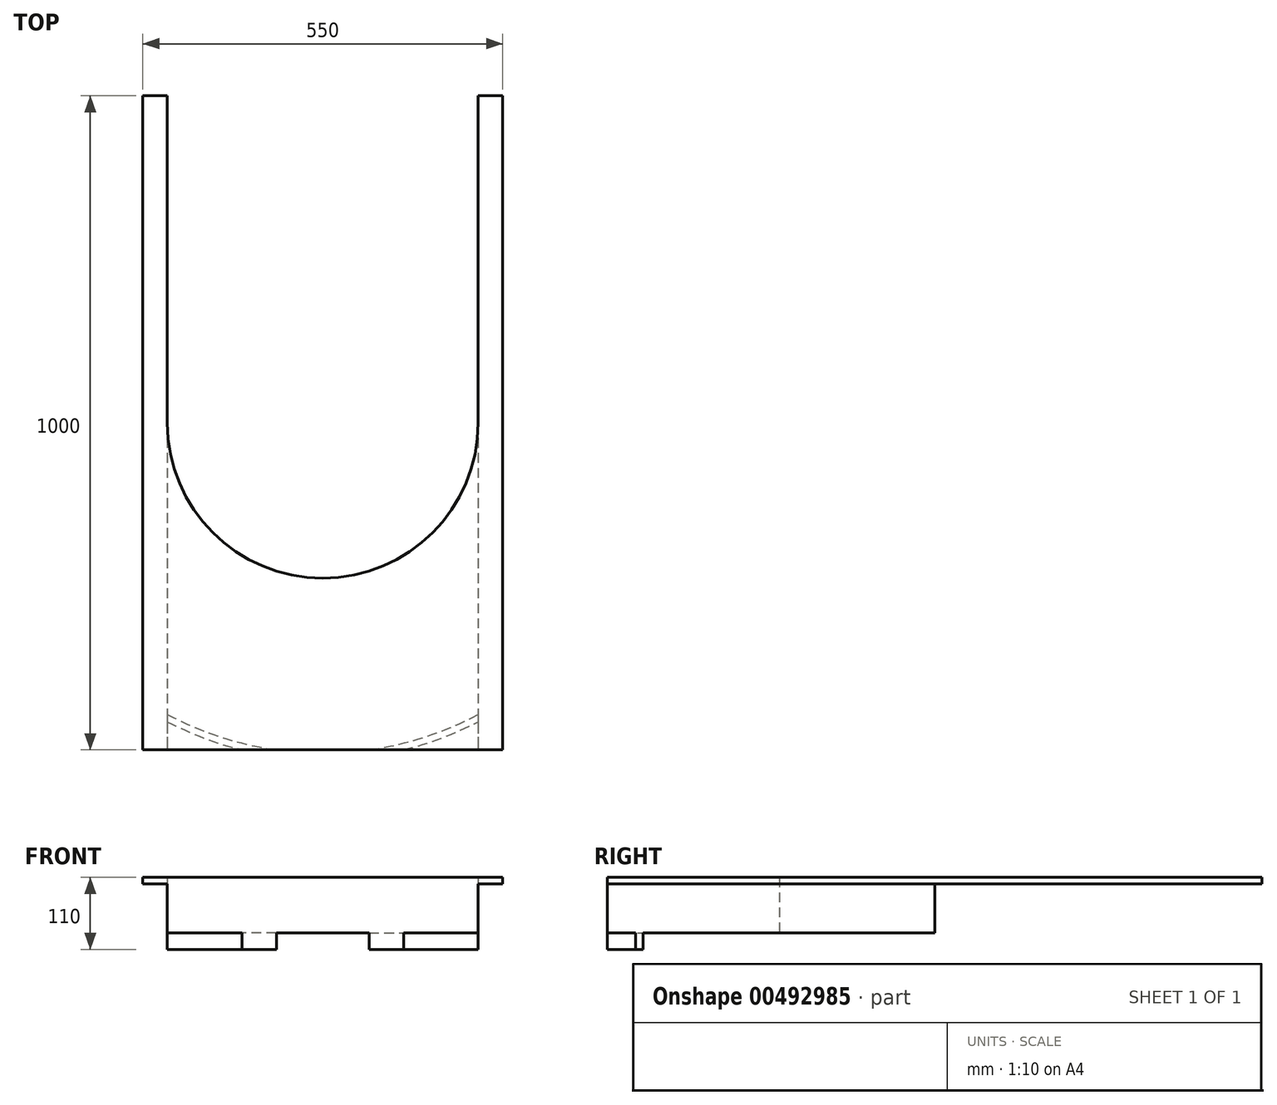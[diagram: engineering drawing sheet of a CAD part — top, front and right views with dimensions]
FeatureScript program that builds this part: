
annotation { "Feature Type Name" : "Feature", "Feature Type Description" : "" }
export const myFeature = defineFeature(function(context is Context, id is Id, definition is map)
    precondition{}
    {
        {
            var Q0;
            Q0=qCreatedBy(makeId("Top.planeOp"),FACE);
            var sketch = newSketch(context, id + "F0", { "sketchPlane" : qUnion([Q0])});
            skArc(sketch, "E0", {"start": v(-237.5, 0) * mm, "mid": v(0, -237.5) * mm, "end": v(237.5, 0) * mm});
            skLineSegment(sketch, "E1.bottom", {"start": v(-275, 500) * mm, "end": v(-237.5, 500) * mm});
            skLineSegment(sketch, "E1.top", {"start": v(-275, -500) * mm, "end": v(275, -500) * mm});
            skLineSegment(sketch, "E1.left", {"start": v(-275, 500) * mm, "end": v(-275, -500) * mm});
            skLineSegment(sketch, "E1.right", {"start": v(275, 500) * mm, "end": v(275, -500) * mm});
            skLineSegment(sketch, "E2", {"start": v(-237.5, 0) * mm, "end": v(-237.5, 500) * mm});
            skLineSegment(sketch, "E3", {"start": v(237.5, 0) * mm, "end": v(237.5, 500) * mm});
            skLineSegment(sketch, "E4.trimOffspring", {"start": v(237.5, 500) * mm, "end": v(275, 500) * mm});
            skSolve(sketch);
        }
        {
            var Q0;
            Q0=makeQuery(id+"F0.imprint","IMPRINT",FACE,{"disambiguationData":[TD([[makeQuery(id+"F0.imprint","IMPRINT",EDGE,{"derivedFrom":sQuery(id+"F0.wireOp",EDGE,"E0")}),-1.0]])]});
            extrude(context, id + "F1", {"entities" : qUnion([Q0]), "depth" : 10 * mm});
        }
        {
            var Q0;
            Q0=makeQuery(id+"F1.opExtrude","CAP_FACE",FACE,{"disambiguationData":[OSD([sQuery(id+"F0.wireOp",EDGE,"E0"),sQuery(id+"F0.wireOp",EDGE,"E1.bottom"),sQuery(id+"F0.wireOp",EDGE,"E1.top"),sQuery(id+"F0.wireOp",EDGE,"E1.left"),sQuery(id+"F0.wireOp",EDGE,"E1.right"),sQuery(id+"F0.wireOp",EDGE,"E2"),sQuery(id+"F0.wireOp",EDGE,"E3"),sQuery(id+"F0.wireOp",EDGE,"E4.trimOffspring")])],"isStart":true});
            var sketch = newSketch(context, id + "F2", { "sketchPlane" : qUnion([Q0])});
            skLineSegment(sketch, "E5", {"start": v(-237.5, 0) * mm, "end": v(-237.5, 500) * mm});
            skLineSegment(sketch, "E6", {"start": v(-237.5, 500) * mm, "end": v(237.5, 500) * mm});
            skLineSegment(sketch, "E7", {"start": v(237.5, 0) * mm, "end": v(237.5, 500) * mm});
            skArc(sketch, "E8", {"start": v(237.5, 0) * mm, "mid": v(0, 237.5) * mm, "end": v(-237.5, 0) * mm});
            skSolve(sketch);
        }
        {
            var Q0;
            Q0 = qSketchRegion(id + "F2", true);
            extrude(context, id + "F3", {"entities" : qUnion([Q0]), "operationType" : NewBodyOperationType.ADD, "depth" : 75 * mm, "offsetDistance" : 25 * mm});
        }
        {
            var Q0;
            Q0=makeQuery(id+"F3.opExtrude","CAP_FACE",FACE,{"disambiguationData":[OSD([sQuery(id+"F2.wireOp",EDGE,"E5"),sQuery(id+"F2.wireOp",EDGE,"E6"),sQuery(id+"F2.wireOp",EDGE,"E7"),sQuery(id+"F2.wireOp",EDGE,"E8")])],"isStart":false});
            var sketch = newSketch(context, id + "F4", { "sketchPlane" : qUnion([Q0])});
            skArc(sketch, "E9", {"start": v(237.5, 445.67) * mm, "mid": v(156.57, 480.12) * mm, "end": v(70.89, 500) * mm});
            skArc(sketch, "E10", {"start": v(237.5, 456.97) * mm, "mid": v(181.72, 481.87) * mm, "end": v(123.39, 500) * mm});
            skLineSegment(sketch, "E11", {"start": v(-237.5, 456.97) * mm, "end": v(-237.5, 445.67) * mm});
            skLineSegment(sketch, "E12", {"start": v(-123.39, 500) * mm, "end": v(-70.89, 500) * mm});
            skLineSegment(sketch, "E13", {"start": v(237.5, 456.97) * mm, "end": v(237.5, 445.67) * mm});
            skArc(sketch, "E14.trimOffspring", {"start": v(-123.39, 500) * mm, "mid": v(-181.72, 481.87) * mm, "end": v(-237.5, 456.97) * mm});
            skArc(sketch, "E15.trimOffspring", {"start": v(-70.89, 500) * mm, "mid": v(-156.57, 480.12) * mm, "end": v(-237.5, 445.67) * mm});
            skLineSegment(sketch, "E16.trimOffspring", {"start": v(70.89, 500) * mm, "end": v(123.39, 500) * mm});
            skSolve(sketch);
        }
        {
            var Q0;
            Q0 = qSketchRegion(id + "F4", true);
            extrude(context, id + "F5", {"entities" : qUnion([Q0]), "operationType" : NewBodyOperationType.ADD, "depth" : 25 * mm, "offsetDistance" : 25 * mm});
        }
    });
